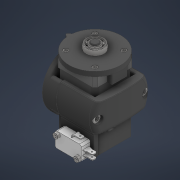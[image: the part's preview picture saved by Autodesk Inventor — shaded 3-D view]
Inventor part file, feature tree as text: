
AUTODESK INVENTOR PART (.ipt)
format: ipt  version: 2022 (Build 260153070, 153G)  size: 1,992,704 bytes
history: native  units: mm
features: other x35, projected_geometry x4, extrude x1, sketch x1
ambient origin geometry x8: Origin, YZ Plane, XZ Plane, XY Plane, X Axis, Y Axis, Z Axis, Center Point
bodies: Solid1 (feature_tree)
feature tree (41):
  other  "shoulder_link.iam"
  other  "Stepper_nema17.ipt:1"
  other  "Rotor_lite.ipt:1"
  other  "DIN 912 - replaced by DIN EN ISO 4762 M4 x 12:1"
  other  "DIN 912 - replaced by DIN EN ISO 4762 M4 x 12:2"
  other  "DIN 912 - replaced by DIN EN ISO 4762 M4 x 12:4"
  other  "DIN 912 - replaced by DIN EN ISO 4762 M4 x 12:3"
  other  "reductor.iam:1::Stator_encoder_lite.ipt:1"
  other  "reductor.iam:1::Center_encoder_lite.ipt:1"
  other  "reductor.iam:1::Excenter_lite.ipt:1"
  other  "reductor.iam:1::Stator_lite.ipt:1"
  other  "reductor.iam:1::Disk_lite.ipt:1"
  other  "reductor.iam:1::DIN 625 - T1 619/8 - 8 x 19 x 6:1"
  other  "reductor.iam:1::Center_lite.ipt:1"
  other  "reductor.iam:1::DIN 625 - T1 619/8 - 8 x 19 x 6:2"
  other  "reductor.iam:1::Rotor_lite.ipt:1"
  other  "reductor.iam:1::Housing_lite.ipt:1"
  other  "reductor.iam:1::Board.ipt:1"
  other  "reductor.iam:1::Magnet.ipt:1"
  other  "Bearing_back_lite.ipt:1"
  other  "DIN 912 - replaced by DIN EN ISO 4762 M3 x 30:1"
  other  "DIN 912 - replaced by DIN EN ISO 4762 M3 x 30:3"
  other  "DIN 912 - replaced by DIN EN ISO 4762 M3 x 30:4"
  other  "DIN 912 - replaced by DIN EN ISO 4762 M3 x 30:2"
  other  "DIN 912 - replaced by DIN EN ISO 4762 M3 x 25:4"
  other  "DIN 912 - replaced by DIN EN ISO 4762 M3 x 25:1"
  other  "DIN 912 - replaced by DIN EN ISO 4762 M3 x 25:2"
  other  "DIN 912 - replaced by DIN EN ISO 4762 M3 x 25:3"
  other  "DIN 625 - T1 619/8 - 8 x 19 x 6:1"
  other  "Stepper_bracket_1_lite.ipt:1"
  other  "DIN 912 - replaced by DIN EN ISO 4762 M5 x 40:1"
  other  "DIN 912 - replaced by DIN EN ISO 4762 M5 x 40:2"
  other  "Limit_switch.ipt:1"
  other  "DIN 912 - replaced by DIN EN ISO 4762 M3 x 12:1"
  other  "DIN 912 - replaced by DIN EN ISO 4762 M3 x 12:2"
  extrude  "Extrusion1"  Depth=10.0mm TaperAngle=0.0deg
  sketch  "Sketch1"  dims[d0=10.0mm d1=10.0mm d2=0.0mm]
  projected_geometry  "Projected Loop1"
  projected_geometry  "Projected Loop2"
  projected_geometry  "Projected Loop3"
  projected_geometry  "Projected Loop4"
